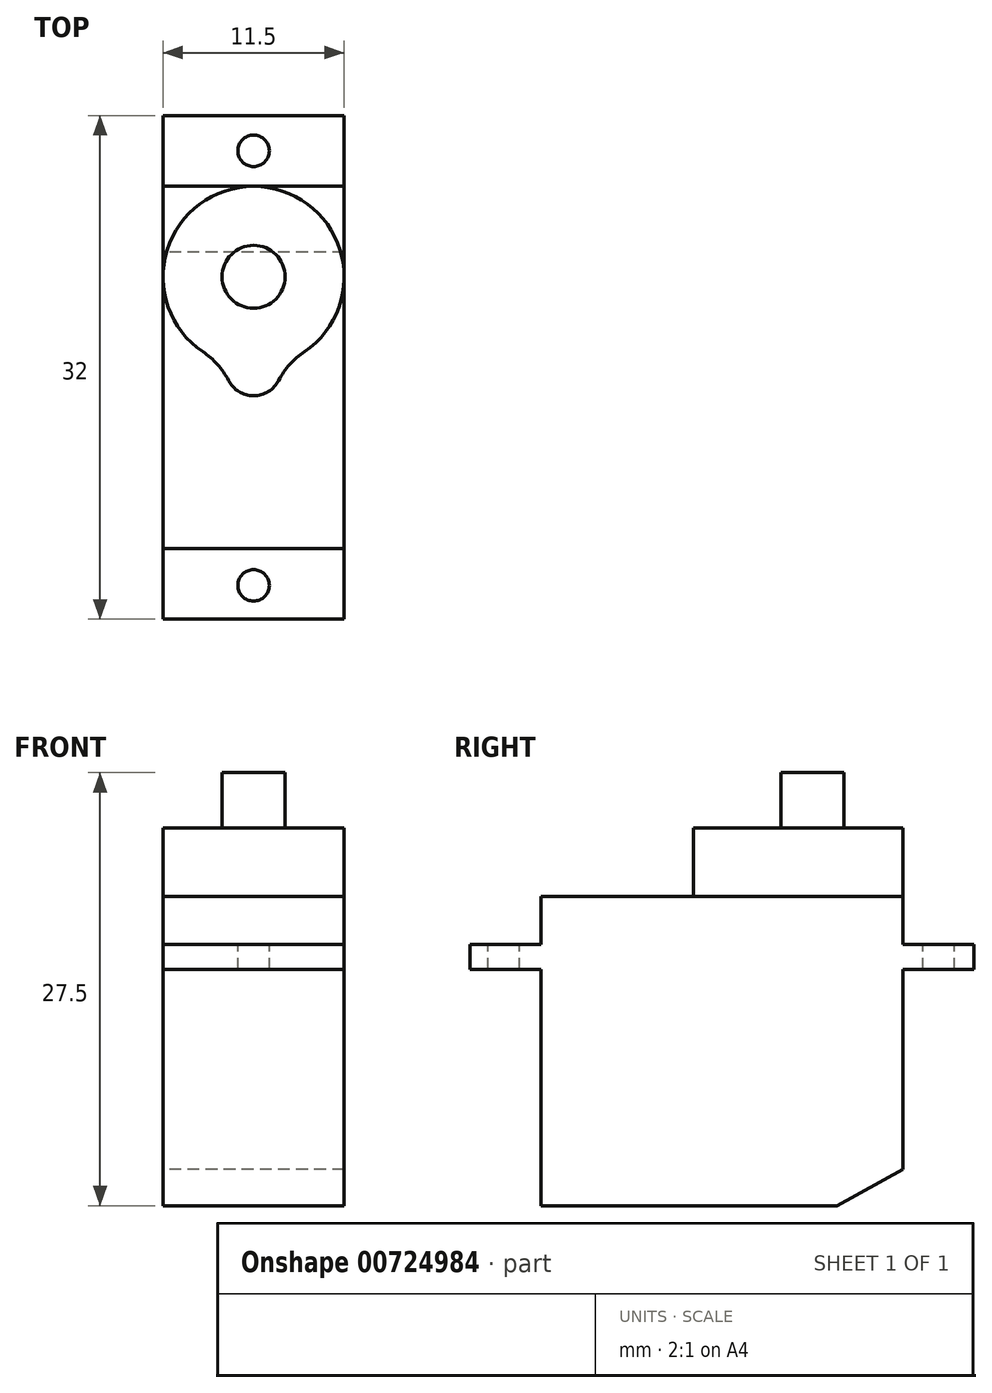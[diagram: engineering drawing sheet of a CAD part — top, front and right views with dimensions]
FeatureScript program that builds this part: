
annotation { "Feature Type Name" : "Feature", "Feature Type Description" : "" }
export const myFeature = defineFeature(function(context is Context, id is Id, definition is map)
    precondition{}
    {
        {
            var Q0;
            Q0=qCreatedBy(makeId("Right.planeOp"),FACE);
            var sketch = newSketch(context, id + "F0", { "sketchPlane" : qUnion([Q0])});
            skLineSegment(sketch, "E0", {"start": v(0, 0) * mm, "end": v(18.8, 0) * mm});
            skLineSegment(sketch, "E1", {"start": v(18.8, 0) * mm, "end": v(23, 2.31) * mm});
            skLineSegment(sketch, "E2", {"start": v(23, 2.31) * mm, "end": v(23, 15) * mm});
            skLineSegment(sketch, "E3", {"start": v(23, 15) * mm, "end": v(27.5, 15) * mm});
            skLineSegment(sketch, "E4", {"start": v(27.5, 15) * mm, "end": v(27.5, 16.6) * mm});
            skLineSegment(sketch, "E5", {"start": v(27.5, 16.6) * mm, "end": v(23, 16.6) * mm});
            skLineSegment(sketch, "E6", {"start": v(23, 16.6) * mm, "end": v(23, 24) * mm});
            skLineSegment(sketch, "E7", {"start": v(23, 24) * mm, "end": v(5, 24) * mm});
            skLineSegment(sketch, "E8", {"start": v(-4.5, 16.6) * mm, "end": v(-4.5, 15) * mm});
            skLineSegment(sketch, "E9", {"start": v(-4.5, 15) * mm, "end": v(0, 15) * mm});
            skLineSegment(sketch, "E10", {"start": v(0, 15) * mm, "end": v(0, 0) * mm});
            skLineSegment(sketch, "E11", {"start": v(5, 24) * mm, "end": v(5, 19.65) * mm});
            skLineSegment(sketch, "E12", {"start": v(5, 19.65) * mm, "end": v(0, 19.65) * mm});
            skLineSegment(sketch, "E13", {"start": v(0, 19.65) * mm, "end": v(0, 16.6) * mm});
            skLineSegment(sketch, "E14", {"start": v(0, 16.6) * mm, "end": v(-4.5, 16.6) * mm});
            skSolve(sketch);
        }
        {
            var Q0;
            Q0 = qSketchRegion(id + "F0", true);
            extrude(context, id + "F1", {"entities" : qUnion([Q0]), "depth" : 11.5 * mm, "offsetDistance" : 25 * mm});
        }
        {
            var Q0;
            Q0=makeQuery(id+"F1.opExtrude","SWEPT_FACE",FACE,{"disambiguationData":[OSD([sQuery(id+"F0.wireOp",EDGE,"E7")])]});
            var sketch = newSketch(context, id + "F2", { "sketchPlane" : qUnion([Q0])});
            skCircle(sketch, "E15", {"center": v(5.75, 17.25) * mm, "radius": 5.75 * mm});
            skPoint(sketch, "E15.centerSnap0", {"position": v(5.75, 23) * mm});
            skCircle(sketch, "E16", {"center": v(5.75, 11.5) * mm, "radius": 1.8 * mm});
            skSolve(sketch);
        }
        {
            var Q0;
            {var subQ4=sQuery(id+"F0.wireOp",EDGE,"E7");var subQ7=makeQuery(id+"F1.opExtrude","SWEPT_EDGE",EDGE,{"disambiguationData":[OSD([subQ4,sQuery(id+"F0.wireOp",EDGE,"E11")])]});Q0=makeQuery(id+"F2.imprint","IMPRINT",FACE,{"disambiguationData":[TD([[makeQuery(id+"F2.imprint","IMPRINT",EDGE,{"derivedFrom":subQ7}),-1.0]])]});}
            var Q1;
            {var subQ0=sQuery(id+"F2.wireOp",EDGE,"E15");var subQ1=sQuery(id+"F0.wireOp",EDGE,"E7");var subQ4=makeQuery(id+"F1.opExtrude","CAP_EDGE",EDGE,{"disambiguationData":[OSD([subQ1])],"isStart":false});var subQ5=makeQuery(id+"F2.imprint","INTERSECT",VERTEX,{"derivedFrom":[subQ4,subQ0]});Q1=makeQuery(id+"F2.imprint","IMPRINT",FACE,{"disambiguationData":[TD([[makeQuery(id+"F2.imprint","IMPRINT",EDGE,{"disambiguationData":[TD([[subQ5,-1.0]])],"derivedFrom":subQ0}),-1.0]])]});}
            var Q2;
            {var subQ0=sQuery(id+"F2.wireOp",EDGE,"E15");var subQ1=sQuery(id+"F0.wireOp",EDGE,"E7");var subQ4=makeQuery(id+"F1.opExtrude","CAP_EDGE",EDGE,{"disambiguationData":[OSD([subQ1])],"isStart":true});var subQ5=makeQuery(id+"F2.imprint","INTERSECT",VERTEX,{"derivedFrom":[subQ4,subQ0]});Q2=makeQuery(id+"F2.imprint","IMPRINT",FACE,{"disambiguationData":[TD([[makeQuery(id+"F2.imprint","IMPRINT",EDGE,{"disambiguationData":[TD([[subQ5,1.0]])],"derivedFrom":subQ0}),-1.0]])]});}
            var Q3;
            Q3=makeQuery(id+"F1.opExtrude","SWEPT_FACE",FACE,{"disambiguationData":[OSD([sQuery(id+"F0.wireOp",EDGE,"E12")])]});
            extrude(context, id + "F3", {"entities" : qUnion([Q0, Q1, Q2]), "operationType" : NewBodyOperationType.REMOVE, "endBound" : BoundingType.UP_TO_SURFACE, "oppositeDirection" : true, "depth" : 25 * mm, "endBoundEntityFace" : qUnion([Q3]), "offsetDistance" : 25 * mm});
        }
        {
            var Q0;
            {var subQ0=sQuery(id+"F2.wireOp",EDGE,"E16");var subQ1=sQuery(id+"F2.wireOp",EDGE,"E15");Q0=makeQuery(id+"F3.boolean.opBoolean","COPY",EDGE,{"derivedFrom":makeQuery(id+"F3.opExtrude","SWEPT_EDGE",EDGE,{"disambiguationData":[OSD([subQ1,subQ0]),TDD([makeQuery(id+"F2.imprint","INTERSECT",VERTEX,{"disambiguationData":[OD(1.0)],"derivedFrom":[subQ1,subQ0]})])]})});}
            var Q1;
            {var subQ0=sQuery(id+"F2.wireOp",EDGE,"E16");var subQ1=sQuery(id+"F2.wireOp",EDGE,"E15");Q1=makeQuery(id+"F3.boolean.opBoolean","COPY",EDGE,{"derivedFrom":makeQuery(id+"F3.opExtrude","SWEPT_EDGE",EDGE,{"disambiguationData":[OSD([subQ1,subQ0]),TDD([makeQuery(id+"F2.imprint","INTERSECT",VERTEX,{"disambiguationData":[OD(0.0)],"derivedFrom":[subQ1,subQ0]})])]})});}
            fillet(context, id + "F4", {"entities" : qUnion([Q0, Q1]), "radius" : 5 * mm, "tangentPropagation" : true, "allowEdgeOverflow" : false});
        }
        {
            var Q0;
            Q0=makeQuery(id+"F1.opExtrude","SWEPT_FACE",FACE,{"disambiguationData":[OSD([sQuery(id+"F0.wireOp",EDGE,"E5")])]});
            var sketch = newSketch(context, id + "F5", { "sketchPlane" : qUnion([Q0])});
            skCircle(sketch, "E17", {"center": v(5.75, 25.25) * mm, "radius": 1 * mm});
            skPoint(sketch, "E17.centerSnap0", {"position": v(5.75, 23) * mm});
            skCircle(sketch, "E18", {"center": v(5.75, -2.35) * mm, "radius": 1 * mm});
            skLineSegment(sketch, "E19", {"start": v(5.75, 27.5) * mm, "end": v(5.75, 23) * mm});
            skSolve(sketch);
        }
        {
            var Q0;
            Q0 = qSketchRegion(id + "F5", true);
            extrude(context, id + "F6", {"entities" : qUnion([Q0]), "operationType" : NewBodyOperationType.REMOVE, "oppositeDirection" : true, "depth" : 25 * mm, "offsetDistance" : 25 * mm});
        }
        {
            var Q0;
            Q0=makeQuery(id+"F1.opExtrude","SWEPT_FACE",FACE,{"disambiguationData":[OSD([sQuery(id+"F0.wireOp",EDGE,"E7")])]});
            var sketch = newSketch(context, id + "F7", { "sketchPlane" : qUnion([Q0])});
            skCircle(sketch, "E20", {"center": v(5.75, 17.25) * mm, "radius": 2 * mm});
            skSolve(sketch);
        }
        {
            var Q0;
            Q0 = qSketchRegion(id + "F7", true);
            extrude(context, id + "F8", {"entities" : qUnion([Q0]), "operationType" : NewBodyOperationType.ADD, "depth" : 3.5 * mm, "offsetDistance" : 25 * mm});
        }
    });
